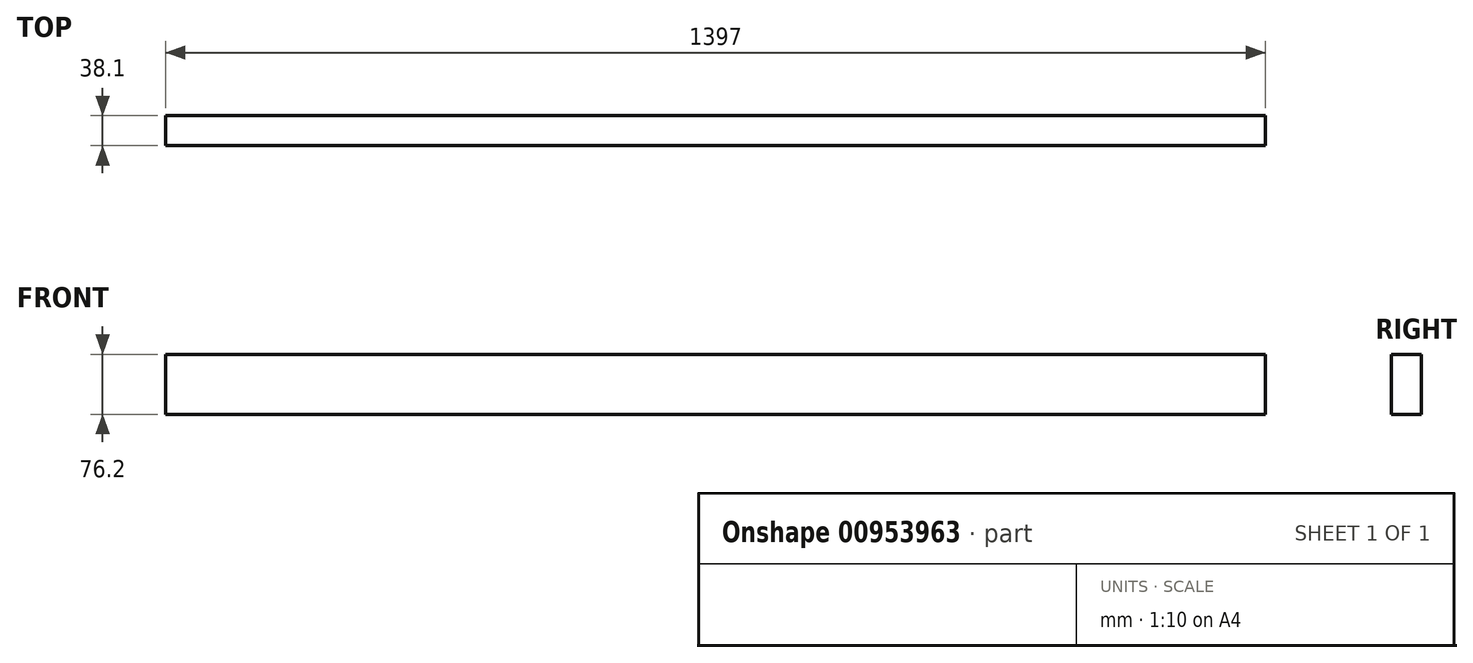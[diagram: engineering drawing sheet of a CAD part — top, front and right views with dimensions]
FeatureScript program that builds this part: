
annotation { "Feature Type Name" : "Feature", "Feature Type Description" : "" }
export const myFeature = defineFeature(function(context is Context, id is Id, definition is map)
    precondition{}
    {
        {
            var Q0;
            Q0=qCreatedBy(makeId("Front.planeOp"),FACE);
            var sketch = newSketch(context, id + "F0", { "sketchPlane" : qUnion([Q0])});
            skLineSegment(sketch, "E0.bottom", {"start": v(0, 0) * mm, "end": v(1397, 0) * mm});
            skLineSegment(sketch, "E0.top", {"start": v(0, 76.2) * mm, "end": v(1397, 76.2) * mm});
            skLineSegment(sketch, "E0.left", {"start": v(0, 0) * mm, "end": v(0, 76.2) * mm});
            skLineSegment(sketch, "E0.right", {"start": v(1397, 0) * mm, "end": v(1397, 76.2) * mm});
            skSolve(sketch);
        }
        {
            var Q0;
            Q0=makeQuery(id+"F0.imprint","IMPRINT",FACE,{"disambiguationData":[TD([[makeQuery(id+"F0.imprint","IMPRINT",EDGE,{"derivedFrom":sQuery(id+"F0.wireOp",EDGE,"E0.bottom")}),1.0]])]});
            extrude(context, id + "F1", {"entities" : qUnion([Q0]), "depth" : 38.1 * mm, "offsetDistance" : 25.4 * mm});
        }
    });
